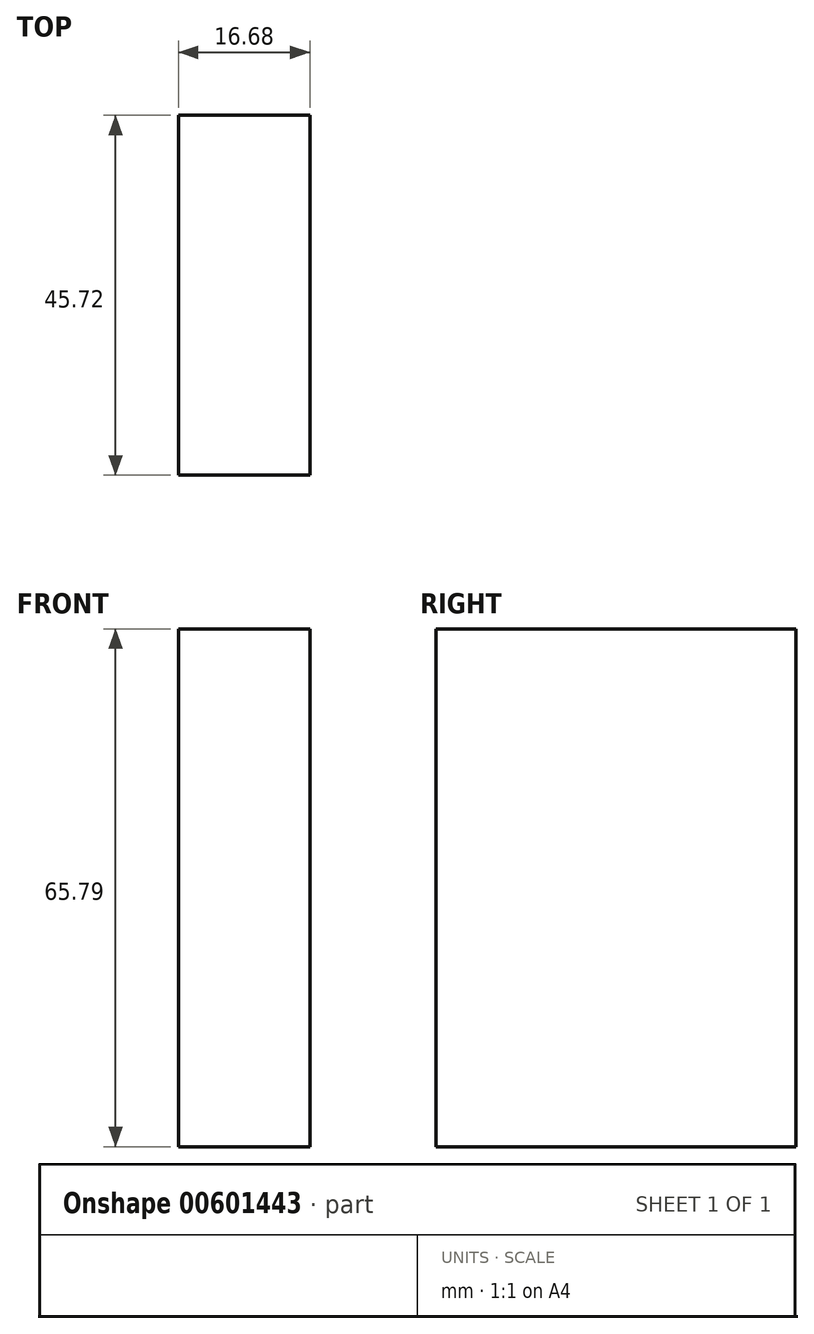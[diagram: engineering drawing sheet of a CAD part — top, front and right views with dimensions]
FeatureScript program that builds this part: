
annotation { "Feature Type Name" : "Feature", "Feature Type Description" : "" }
export const myFeature = defineFeature(function(context is Context, id is Id, definition is map)
    precondition{}
    {
        {
            var Q0;
            Q0=qCreatedBy(makeId("Top.planeOp"),FACE);
            var sketch = newSketch(context, id + "F0", { "sketchPlane" : qUnion([Q0])});
            skLineSegment(sketch, "E0.bottom", {"start": v(0, 0) * mm, "end": v(-16.68, 0) * mm});
            skLineSegment(sketch, "E0.top", {"start": v(0, 45.72) * mm, "end": v(-16.68, 45.72) * mm});
            skLineSegment(sketch, "E0.left", {"start": v(0, 0) * mm, "end": v(0, 45.72) * mm});
            skLineSegment(sketch, "E0.right", {"start": v(-16.68, 0) * mm, "end": v(-16.68, 45.72) * mm});
            skSolve(sketch);
        }
        {
            var Q0;
            Q0 = qSketchRegion(id + "F0", true);
            extrude(context, id + "F1", {"entities" : qUnion([Q0]), "depth" : 65.8 * mm, "offsetDistance" : 25.4 * mm});
        }
    });
